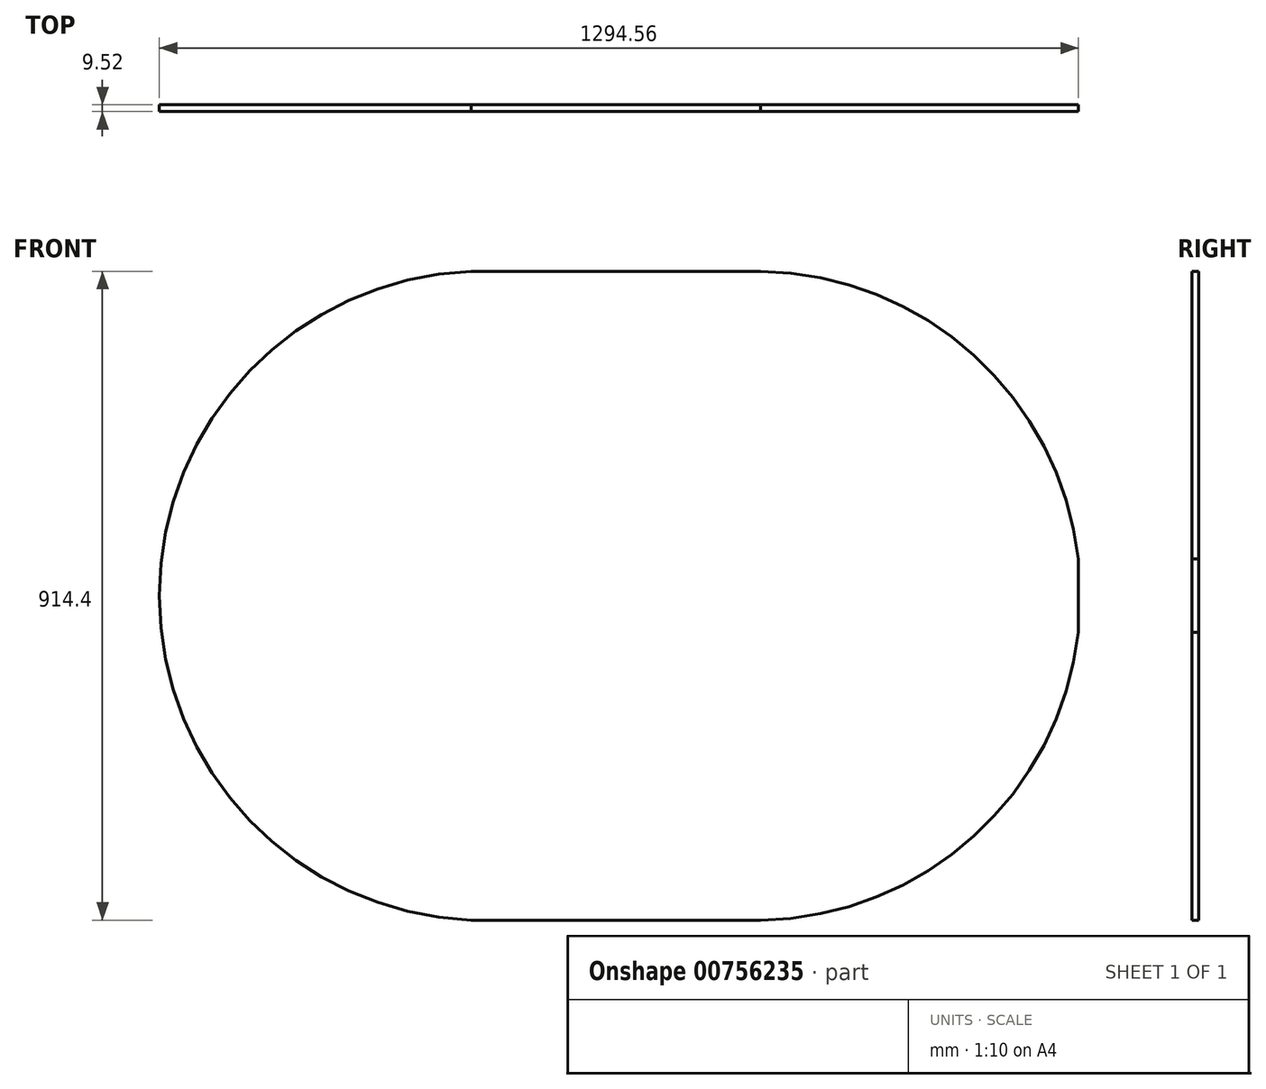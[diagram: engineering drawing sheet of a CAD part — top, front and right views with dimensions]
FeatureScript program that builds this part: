
annotation { "Feature Type Name" : "Feature", "Feature Type Description" : "" }
export const myFeature = defineFeature(function(context is Context, id is Id, definition is map)
    precondition{}
    {
        {
            var Q0;
            Q0=qCreatedBy(makeId("Front.planeOp"),FACE);
            var sketch = newSketch(context, id + "F0", { "sketchPlane" : qUnion([Q0])});
            skLineSegment(sketch, "E0.bottom", {"start": v(-647.7, -457.2) * mm, "end": v(647.7, -457.2) * mm});
            skLineSegment(sketch, "E0.top", {"start": v(-647.7, 457.2) * mm, "end": v(647.7, 457.2) * mm});
            skLineSegment(sketch, "E0.left", {"start": v(-647.7, -457.2) * mm, "end": v(-647.7, 457.2) * mm});
            skLineSegment(sketch, "E0.right", {"start": v(647.7, -457.2) * mm, "end": v(647.7, 457.2) * mm});
            skPoint(sketch, "E0.middle", {"position": v(0, 0) * mm});
            skArc(sketch, "E1", {"start": v(-207.83, 457.2) * mm, "mid": v(-646.74, -10.8) * mm, "end": v(-186.22, -457.57) * mm});
            skArc(sketch, "E2", {"start": v(200.11, 457.2) * mm, "mid": v(650.62, 0) * mm, "end": v(200.11, -457.2) * mm});
            skSolve(sketch);
        }
        {
            var Q0;
            {var subQ3=sQuery(id+"F0.wireOp",EDGE,"E0.bottom");var subQ5=sQuery(id+"F0.wireOp",EDGE,"E2");var subQ10=makeQuery(id+"F0.imprint","INTERSECT",VERTEX,{"derivedFrom":[subQ3,subQ5]});Q0=makeQuery(id+"F0.imprint","IMPRINT",FACE,{"disambiguationData":[TD([[makeQuery(id+"F0.imprint","IMPRINT",EDGE,{"disambiguationData":[TD([[subQ10,1.0]])],"derivedFrom":subQ3}),1.0]])]});}
            extrude(context, id + "F1", {"entities" : qUnion([Q0]), "endBound" : BoundingType.SYMMETRIC, "depth" : 9.52 * mm, "offsetDistance" : 25.4 * mm});
        }
    });
